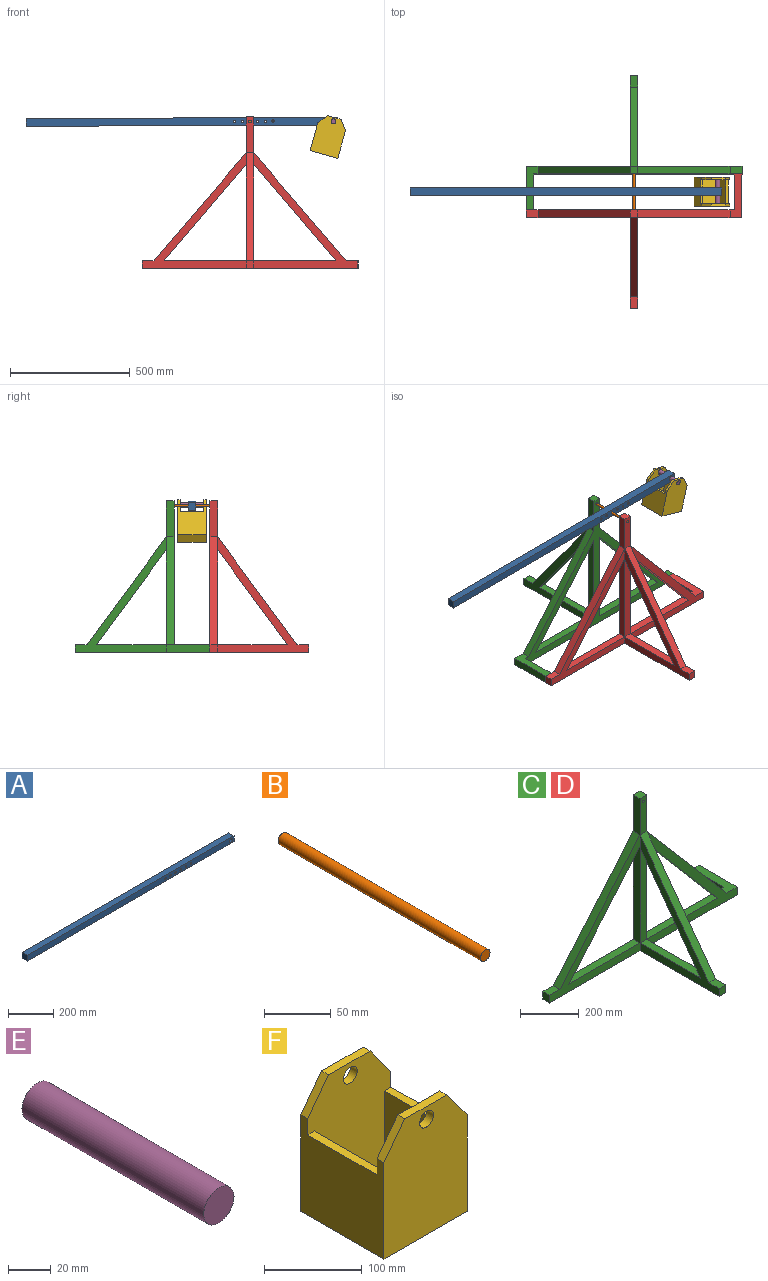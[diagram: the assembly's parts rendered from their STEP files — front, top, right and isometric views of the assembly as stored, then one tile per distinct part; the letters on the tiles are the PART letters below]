
ASSEMBLY  parts=6 mates=5
PART A: 13 faces, bbox 1300x32x32 mm
  f0: plane 1300x32mm, normal (0,0,1), area 41600mm2, adj f1,f3,f4,f5
  f1: plane 1300x32mm, normal (0,-1,0), area 40814.6mm2, adj f0,f2,f4,f5,f6,f7,f8,f9
  f2: plane 1300x32mm, normal (0,0,-1), area 41600mm2, adj f1,f3,f4,f5
  f3: plane 1300x32mm, normal (0,1,0), area 40814.6mm2, adj f0,f2,f4,f5,f6,f7,f8,f9
  f4: plane 32x32mm, normal (1,0,0), area 1024mm2, adj f0,f1,f2,f3
  f5: plane 32x32mm, normal (-1,0,0), area 1024mm2, adj f0,f1,f2,f3
  f6: cylinder r=5mm len=32mm, axis (0,1,0), area 1005.3mm2, adj f1,f3
  f7: cylinder r=5mm len=32mm, axis (0,1,0), area 1005.3mm2, adj f1,f3
  f8: cylinder r=5mm len=32mm, axis (0,1,0), area 1005.3mm2, adj f1,f3
  f9: cylinder r=5mm len=32mm, axis (0,1,0), area 1005.3mm2, adj f1,f3
  f10: cylinder r=5mm len=32mm, axis (0,1,0), area 1005.3mm2, adj f1,f3
  f11: cylinder r=5mm len=32mm, axis (0,1,0), area 1005.3mm2, adj f1,f3
  f12: cylinder r=10mm len=32mm, axis (0,1,0), area 2010.6mm2, adj f1,f3
PART B: 3 faces, bbox 10x214x10 mm
  f0: cylinder r=5mm len=214mm, axis (0,1,0), area 6723mm2, adj f1,f2
  f1: plane 10x10mm, normal (0,-1,0), area 78.5mm2, adj f0
  f2: plane 10x10mm, normal (0,1,0), area 78.5mm2, adj f0
PART C: 29 faces, bbox 900x562x632 mm
  f0: plane 482x434mm, normal (0,-1,0), area 31781.4mm2, adj f7,f8,f9,f11,f13,f18,f19
  f1: plane 150x32mm, normal (0,-1,0), area 4721.5mm2, adj f15,f16,f17,f24,f28
  f2: plane 482x434mm, normal (0,-1,0), area 31781.4mm2, adj f5,f6,f10,f11,f14,f20,f21
  f3: plane 290.32x32mm, normal (0,0,1), area 9290.2mm2, adj f4,f6,f8,f25
  f4: plane 395.89x32mm, normal (0,-1,0), area 12668.4mm2, adj f3,f6,f8,f25
  f5: plane 341.93x32mm, normal (0,0,1), area 10941.8mm2, adj f2,f6,f12,f21
  f6: plane 482x412mm, normal (1,0,0), area 41765.9mm2, adj f2,f3,f4,f5,f11,f12,f21,f22
  f7: plane 50x32mm, normal (0,0,1), area 1600mm2, adj f0,f12,f13,f18
  f8: plane 482x412mm, normal (-1,0,0), area 41765.9mm2, adj f0,f3,f4,f9,f11,f12,f19,f22
  f9: plane 341.93x32mm, normal (0,0,1), area 10941.8mm2, adj f0,f8,f12,f19
  f10: plane 182x50mm, normal (0,0,1), area 6400mm2, adj f2,f12,f14,f20,f26,f27
  f11: plane 900x562mm, normal (0,0,-1), area 45760mm2, adj f0,f2,f6,f8,f12,f13,f14,f23
  f12: plane 868x632mm, normal (0,1,0), area 82684.2mm2, adj f5,f6,f7,f8,f9,f10,f11,f13
  f13: plane 32x32mm, normal (-1,0,0), area 1024mm2, adj f0,f7,f11,f12
  f14: plane 182x32mm, normal (1,0,0), area 5824mm2, adj f2,f10,f11,f27
  f15: plane 150x32mm, normal (-1,0,0), area 4800mm2, adj f1,f12,f17,f18
  f16: plane 150x32mm, normal (1,0,0), area 4800mm2, adj f1,f12,f17,f20
  f17: plane 32x32mm, normal (0,0,1), area 1024mm2, adj f1,f12,f15,f16
  f18: plane 450x384mm, normal (-0.76,0,0.65), area 18930.3mm2, adj f0,f7,f12,f15
  f19: plane 400.7x341.93mm, normal (0.76,0,-0.65), area 16856.5mm2, adj f0,f8,f9,f12
  f20: plane 450x384mm, normal (0.76,0,0.65), area 18930.3mm2, adj f2,f10,f12,f16
  f21: plane 400.7x341.93mm, normal (-0.76,0,-0.65), area 16856.5mm2, adj f2,f5,f6,f12
  f22: plane 50x32mm, normal (0,0,1), area 1600mm2, adj f6,f8,f23,f24
  f23: plane 32x32mm, normal (0,-1,0), area 1024mm2, adj f6,f8,f11,f22
  f24: plane 450x330mm, normal (0,-0.81,0.59), area 17857mm2, adj f1,f6,f8,f22
  f25: plane 395.89x290.32mm, normal (0,0.81,-0.59), area 15709.7mm2, adj f3,f4,f6,f8
  f26: plane 150x32mm, normal (-1,0,0), area 4800mm2, adj f10,f11,f12,f27
  f27: plane 32x32mm, normal (0,1,0), area 1024mm2, adj f10,f11,f14,f26
  f28: cylinder r=5mm len=32mm, axis (0,1,0), area 1005.3mm2, adj f1,f12
PART D: same geometry as C
PART E: 3 faces, bbox 20x120x20 mm
  f0: cylinder r=10mm len=120mm, axis (0,1,0), area 7539.8mm2, adj f1,f2
  f1: plane 20x20mm, normal (0,-1,0), area 314.2mm2, adj f0
  f2: plane 20x20mm, normal (0,1,0), area 314.2mm2, adj f0
PART F: 20 faces, bbox 120x120x160 mm
  f0: plane 160x120mm, normal (0,-1,0), area 17685.8mm2, adj f1,f3,f4,f13,f14,f15,f17
  f1: plane 120x120mm, normal (0,0,-1), area 14400mm2, adj f0,f2,f3,f4
  f2: plane 160x120mm, normal (0,1,0), area 17685.8mm2, adj f1,f3,f4,f10,f11,f12,f16
  f3: plane 120x120mm, normal (1,0,0), area 12400mm2, adj f0,f1,f2,f5,f7,f10,f13,f19
  f4: plane 120x120mm, normal (-1,0,0), area 12400mm2, adj f0,f1,f2,f5,f7,f11,f15,f18
  f5: plane 150x120mm, normal (0,1,0), area 14685.8mm2, adj f3,f4,f6,f8,f9,f13,f14,f15
  f6: plane 100x100mm, normal (0,0,1), area 10000mm2, adj f5,f7,f8,f9
  f7: plane 150x120mm, normal (0,-1,0), area 14685.8mm2, adj f3,f4,f6,f8,f9,f10,f11,f12
  f8: plane 100x90mm, normal (-1,0,0), area 9000mm2, adj f5,f6,f7,f19
  f9: plane 100x90mm, normal (1,0,0), area 9000mm2, adj f5,f6,f7,f18
  f10: plane 40x30mm, normal (0.8,0,0.6), area 500mm2, adj f2,f3,f7,f12
  f11: plane 40x30mm, normal (-0.8,0,0.6), area 500mm2, adj f2,f4,f7,f12
  f12: plane 60x10mm, normal (0,0,1), area 600mm2, adj f2,f7,f10,f11
  f13: plane 40x30mm, normal (0.8,0,0.6), area 500mm2, adj f0,f3,f5,f14
  f14: plane 60x10mm, normal (0,0,1), area 600mm2, adj f0,f5,f13,f15
  f15: plane 40x30mm, normal (-0.8,0,0.6), area 500mm2, adj f0,f4,f5,f14
  f16: cylinder r=10mm len=20mm, axis (0,1,0), area 628.3mm2, adj f2,f7
  f17: cylinder r=10mm len=20mm, axis (0,1,0), area 628.3mm2, adj f0,f5
  f18: plane 100x10mm, normal (0,0,1), area 1000mm2, adj f4,f5,f7,f9
  f19: plane 100x10mm, normal (0,0,1), area 1000mm2, adj f3,f5,f7,f8
PLACE A rot(axis=(0,-1,0),0.2deg) t=(-668.04,12.89,213.44)mm
PLACE B rot(axis=(0,1,0),31.2deg) t=(-368.1,157.94,418.21)mm
PLACE C rot(axis=(0,0,1),180deg) t=(-386.07,232.94,-53.75)mm fixed
PLACE D t=(-386.07,82.94,-53.75)mm
PLACE E rot(axis=(0,-1,0),44.9deg) t=(-131.56,217.94,123.95)mm
PLACE F rot(axis=(0,1,0),15.6deg) t=(-166.14,-155.66,328.31)mm
MATE fastened C.f27 <-> D.f12  axis (0,-1,0) through (-836.07,82.94,-21.75)mm
MATE revolute A.f6 <-> B.f0  axis (0,1,0) through (-386.07,157.94,558.63)mm
MATE revolute F.f16 <-> E.f0  axis (0,1,0) through (-38.02,217.94,559.6)mm
MATE revolute E.f0 <-> A.f12  axis (0,1,0) through (-38.02,157.94,559.6)mm
MATE revolute B.f0 <-> C.f28  axis (0,1,0) through (-386.07,264.94,558.63)mm
